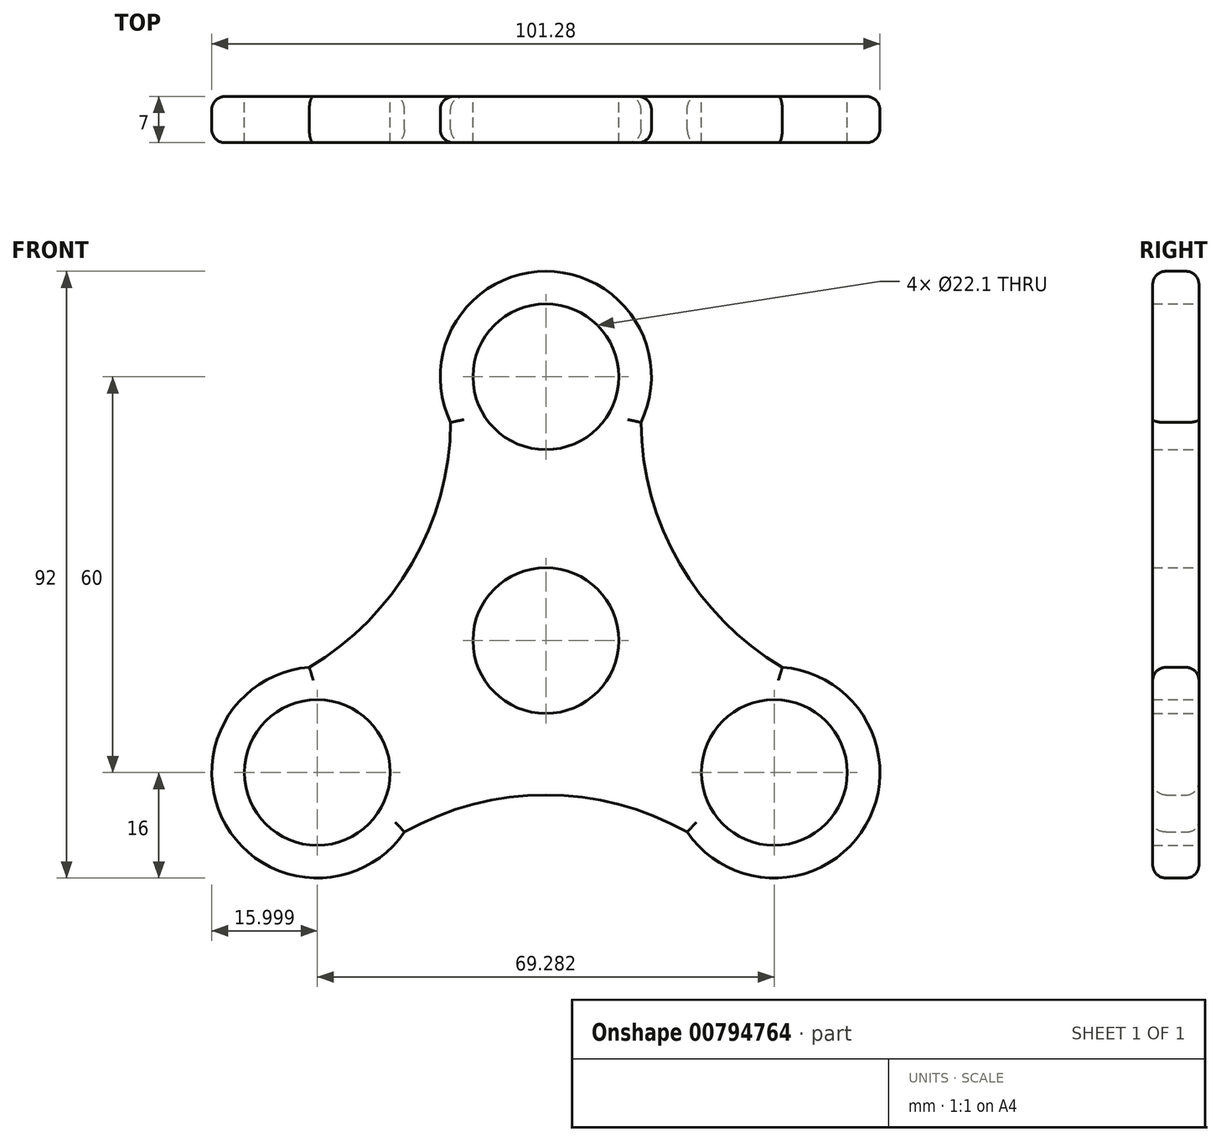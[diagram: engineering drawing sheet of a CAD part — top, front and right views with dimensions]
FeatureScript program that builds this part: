
annotation { "Feature Type Name" : "Feature", "Feature Type Description" : "" }
export const myFeature = defineFeature(function(context is Context, id is Id, definition is map)
    precondition{}
    {
        {
            var Q0;
            Q0=qCreatedBy(makeId("Front.planeOp"),FACE);
            var sketch = newSketch(context, id + "F0", { "sketchPlane" : qUnion([Q0])});
            skCircle(sketch, "E0", {"center": v(0, 0) * mm, "radius": 11.05 * mm});
            skCircle(sketch, "E1", {"center": v(0, 40) * mm, "radius": 11.05 * mm});
            skCircle(sketch, "E2.1.0", {"center": v(-34.64, -20) * mm, "radius": 11.05 * mm});
            skCircle(sketch, "E2.2.0", {"center": v(34.64, -20) * mm, "radius": 11.05 * mm});
            skCircle(sketch, "E3", {"center": v(0, 40) * mm, "radius": 16 * mm});
            skCircle(sketch, "E4.1.0", {"center": v(-34.64, -20) * mm, "radius": 16 * mm});
            skCircle(sketch, "E4.2.0", {"center": v(34.64, -20) * mm, "radius": 16 * mm});
            skArc(sketch, "E5", {"start": v(14.42, 33.07) * mm, "mid": v(20.27, 11.7) * mm, "end": v(35.85, -4.05) * mm});
            skArc(sketch, "E6.1.0", {"start": v(-35.85, -4.05) * mm, "mid": v(-20.27, 11.7) * mm, "end": v(-14.42, 33.07) * mm});
            skArc(sketch, "E6.2.0", {"start": v(21.43, -29.03) * mm, "mid": v(0, -23.4) * mm, "end": v(-21.43, -29.03) * mm});
            skSolve(sketch);
        }
        {
            var Q0;
            Q0=makeQuery(id+"F0.imprint","IMPRINT",FACE,{"disambiguationData":[TD([[makeQuery(id+"F0.imprint","IMPRINT",EDGE,{"derivedFrom":sQuery(id+"F0.wireOp",EDGE,"E2.1.0")}),-1.0]])]});
            var Q1;
            Q1=makeQuery(id+"F0.imprint","IMPRINT",FACE,{"disambiguationData":[TD([[makeQuery(id+"F0.imprint","IMPRINT",EDGE,{"derivedFrom":sQuery(id+"F0.wireOp",EDGE,"E0")}),-1.0]])]});
            var Q2;
            Q2=makeQuery(id+"F0.imprint","IMPRINT",FACE,{"disambiguationData":[TD([[makeQuery(id+"F0.imprint","IMPRINT",EDGE,{"derivedFrom":sQuery(id+"F0.wireOp",EDGE,"E1")}),-1.0]])]});
            var Q3;
            Q3=makeQuery(id+"F0.imprint","IMPRINT",FACE,{"disambiguationData":[TD([[makeQuery(id+"F0.imprint","IMPRINT",EDGE,{"derivedFrom":sQuery(id+"F0.wireOp",EDGE,"E2.2.0")}),-1.0]])]});
            extrude(context, id + "F1", {"entities" : qUnion([Q0, Q1, Q2, Q3]), "depth" : 7 * mm, "offsetDistance" : 25 * mm});
        }
        {
            var Q0;
            Q0=makeQuery(id+"F1.opExtrude","CAP_EDGE",EDGE,{"disambiguationData":[OSD([sQuery(id+"F0.wireOp",EDGE,"E6.2.0")])],"isStart":true});
            var Q1;
            Q1=makeQuery(id+"F1.opExtrude","CAP_EDGE",EDGE,{"disambiguationData":[OSD([sQuery(id+"F0.wireOp",EDGE,"E4.2.0")])],"isStart":true});
            var Q2;
            Q2=makeQuery(id+"F1.opExtrude","CAP_EDGE",EDGE,{"disambiguationData":[OSD([sQuery(id+"F0.wireOp",EDGE,"E5")])],"isStart":true});
            var Q3;
            Q3=makeQuery(id+"F1.opExtrude","CAP_EDGE",EDGE,{"disambiguationData":[OSD([sQuery(id+"F0.wireOp",EDGE,"E3")])],"isStart":true});
            var Q4;
            Q4=makeQuery(id+"F1.opExtrude","CAP_EDGE",EDGE,{"disambiguationData":[OSD([sQuery(id+"F0.wireOp",EDGE,"E6.1.0")])],"isStart":true});
            var Q5;
            Q5=makeQuery(id+"F1.opExtrude","CAP_EDGE",EDGE,{"disambiguationData":[OSD([sQuery(id+"F0.wireOp",EDGE,"E4.1.0")])],"isStart":true});
            var Q6;
            Q6=makeQuery(id+"F1.opExtrude","CAP_EDGE",EDGE,{"disambiguationData":[OSD([sQuery(id+"F0.wireOp",EDGE,"E3")])],"isStart":false});
            var Q7;
            Q7=makeQuery(id+"F1.opExtrude","CAP_EDGE",EDGE,{"disambiguationData":[OSD([sQuery(id+"F0.wireOp",EDGE,"E5")])],"isStart":false});
            var Q8;
            Q8=makeQuery(id+"F1.opExtrude","CAP_EDGE",EDGE,{"disambiguationData":[OSD([sQuery(id+"F0.wireOp",EDGE,"E4.2.0")])],"isStart":false});
            var Q9;
            Q9=makeQuery(id+"F1.opExtrude","CAP_EDGE",EDGE,{"disambiguationData":[OSD([sQuery(id+"F0.wireOp",EDGE,"E6.2.0")])],"isStart":false});
            var Q10;
            Q10=makeQuery(id+"F1.opExtrude","CAP_EDGE",EDGE,{"disambiguationData":[OSD([sQuery(id+"F0.wireOp",EDGE,"E4.1.0")])],"isStart":false});
            var Q11;
            Q11=makeQuery(id+"F1.opExtrude","CAP_EDGE",EDGE,{"disambiguationData":[OSD([sQuery(id+"F0.wireOp",EDGE,"E6.1.0")])],"isStart":false});
            fillet(context, id + "F2", {"entities" : qUnion([Q0, Q1, Q2, Q3, Q4, Q5, Q6, Q7, Q8, Q9, Q10, Q11]), "radius" : 2 * mm, "tangentPropagation" : true, "allowEdgeOverflow" : false});
        }
    });
